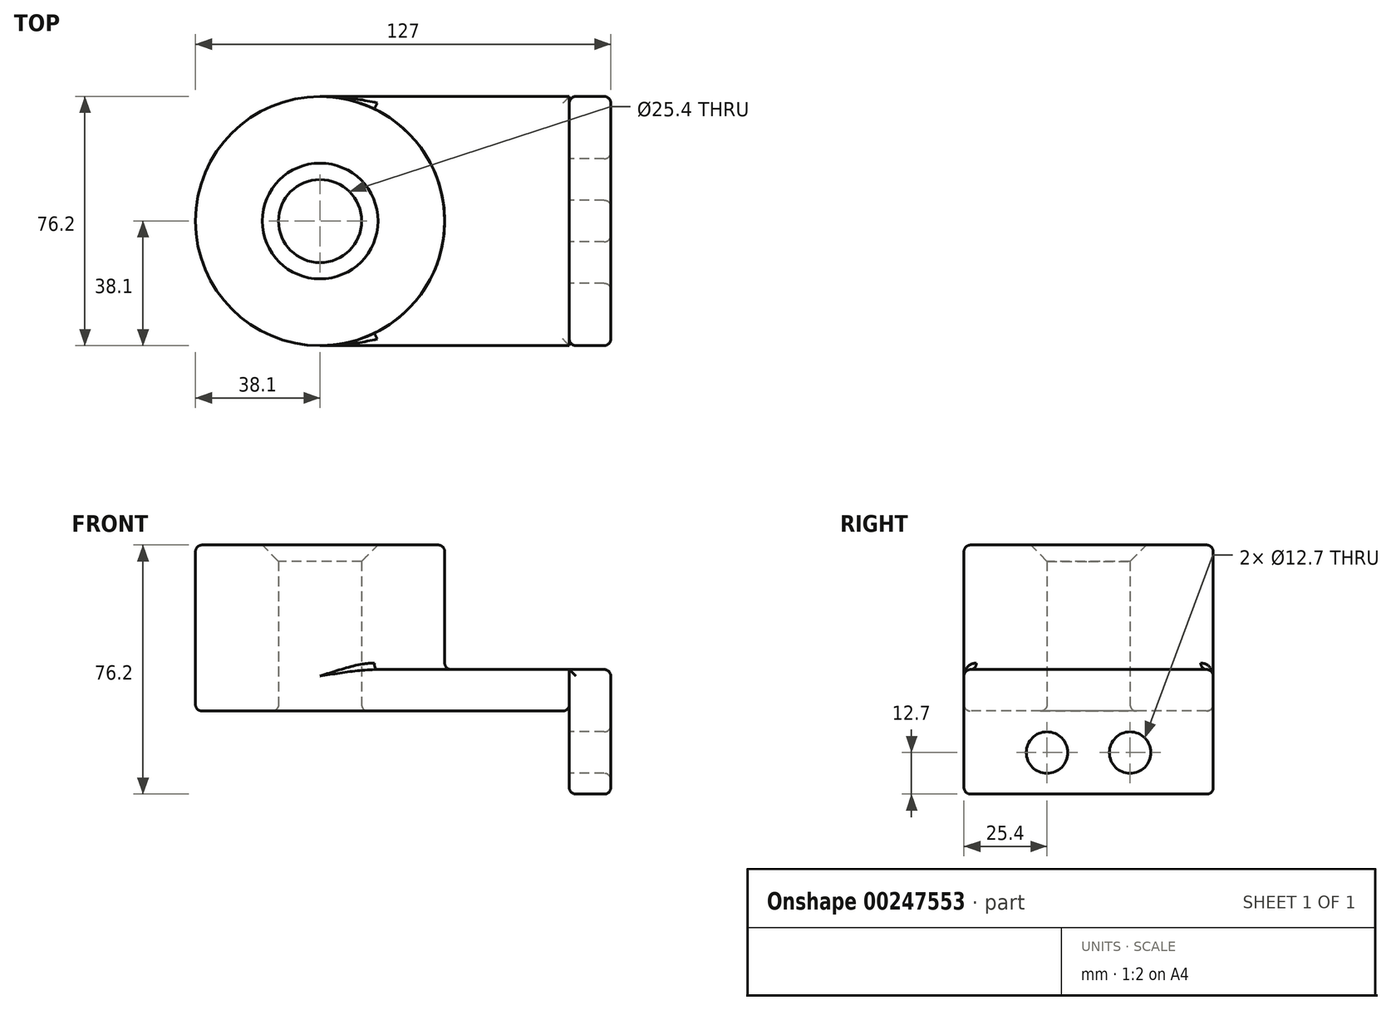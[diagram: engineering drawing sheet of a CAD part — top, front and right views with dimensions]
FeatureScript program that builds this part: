
annotation { "Feature Type Name" : "Feature", "Feature Type Description" : "" }
export const myFeature = defineFeature(function(context is Context, id is Id, definition is map)
    precondition{}
    {
        {
            var Q0;
            Q0=qCreatedBy(makeId("Top.planeOp"),FACE);
            var sketch = newSketch(context, id + "F0", { "sketchPlane" : qUnion([Q0])});
            skLineSegment(sketch, "E0.bottom", {"start": v(38.1, 38.1) * mm, "end": v(-38.1, 38.1) * mm});
            skLineSegment(sketch, "E0.top", {"start": v(38.1, -38.1) * mm, "end": v(-38.1, -38.1) * mm});
            skLineSegment(sketch, "E0.left", {"start": v(38.1, 38.1) * mm, "end": v(38.1, -38.1) * mm});
            skLineSegment(sketch, "E0.right", {"start": v(-38.1, 38.1) * mm, "end": v(-38.1, -38.1) * mm});
            skPoint(sketch, "E0.middle", {"position": v(0, 0) * mm});
            skCircle(sketch, "E1", {"center": v(-38.1, 0) * mm, "radius": 38.1 * mm});
            skCircle(sketch, "E2", {"center": v(-38.1, 0) * mm, "radius": 12.7 * mm});
            skSolve(sketch);
        }
        {
            var Q0;
            Q0 = qSketchRegion(id + "F0", true);
            extrude(context, id + "F1", {"entities" : qUnion([Q0]), "depth" : 12.7 * mm});
        }
        {
            var Q0;
            {var subQ1=sQuery(id+"F0.wireOp",EDGE,"E0.right");var subQ3=sQuery(id+"F0.wireOp",EDGE,"E2");var subQ4=makeQuery(id+"F0.imprint","INTERSECT",VERTEX,{"disambiguationData":[OD(0.0)],"derivedFrom":[subQ1,subQ3]});Q0=makeQuery(id+"F0.imprint","IMPRINT",FACE,{"disambiguationData":[TD([[makeQuery(id+"F0.imprint","IMPRINT",EDGE,{"disambiguationData":[TD([[subQ4,1.0]])],"derivedFrom":subQ3}),-1.0]])]});}
            var Q1;
            {var subQ1=sQuery(id+"F0.wireOp",EDGE,"E0.right");var subQ3=sQuery(id+"F0.wireOp",EDGE,"E2");var subQ4=makeQuery(id+"F0.imprint","INTERSECT",VERTEX,{"disambiguationData":[OD(0.0)],"derivedFrom":[subQ1,subQ3]});Q1=makeQuery(id+"F0.imprint","IMPRINT",FACE,{"disambiguationData":[TD([[makeQuery(id+"F0.imprint","IMPRINT",EDGE,{"disambiguationData":[TD([[subQ4,-1.0]])],"derivedFrom":subQ3}),-1.0]])]});}
            extrude(context, id + "F2", {"entities" : qUnion([Q0, Q1]), "operationType" : NewBodyOperationType.ADD, "depth" : 50.8 * mm});
        }
        {
            var Q0;
            Q0=makeQuery(id+"F1.opExtrude","SWEPT_FACE",FACE,{"disambiguationData":[OSD([sQuery(id+"F0.wireOp",EDGE,"E0.left")])]});
            var sketch = newSketch(context, id + "F3", { "sketchPlane" : qUnion([Q0])});
            skLineSegment(sketch, "E3.bottom", {"start": v(-38.1, 12.7) * mm, "end": v(38.1, 12.7) * mm});
            skLineSegment(sketch, "E3.top", {"start": v(-38.1, -25.4) * mm, "end": v(38.1, -25.4) * mm});
            skLineSegment(sketch, "E3.left", {"start": v(-38.1, 12.7) * mm, "end": v(-38.1, -25.4) * mm});
            skLineSegment(sketch, "E3.right", {"start": v(38.1, 12.7) * mm, "end": v(38.1, -25.4) * mm});
            skLineSegment(sketch, "E4", {"start": v(0, 12.7) * mm, "end": v(0, -52.81) * mm, "construction": true});
            skPoint(sketch, "E4.endSnap0", {"position": v(0, 12.7) * mm});
            skCircle(sketch, "E5", {"center": v(-12.7, -12.7) * mm, "radius": 6.35 * mm});
            skCircle(sketch, "E6.MirrorC", {"center": v(12.7, -12.7) * mm, "radius": 6.35 * mm});
            skSolve(sketch);
        }
        {
            var Q0;
            {var subQ2=sQuery(id+"F3.wireOp",EDGE,"E3.top");Q0=makeQuery(id+"F3.imprint","IMPRINT",FACE,{"disambiguationData":[TD([[makeQuery(id+"F3.imprint","IMPRINT",EDGE,{"derivedFrom":subQ2}),1.0]])]});}
            var Q1;
            {var subQ0=sQuery(id+"F3.wireOp",EDGE,"E3.bottom");Q1=makeQuery(id+"F3.imprint","IMPRINT",FACE,{"disambiguationData":[TD([[makeQuery(id+"F3.imprint","IMPRINT",EDGE,{"derivedFrom":subQ0}),1.0]])]});}
            extrude(context, id + "F4", {"entities" : qUnion([Q0, Q1]), "depth" : 12.7 * mm});
        }
        {
            var Q0;
            Q0=makeQuery(id+"F1.opExtrude","CAP_EDGE",EDGE,{"disambiguationData":[OSD([sQuery(id+"F0.wireOp",EDGE,"E0.top")])],"isStart":false});
            var Q1;
            Q1=makeQuery(id+"F1.opExtrude","CAP_EDGE",EDGE,{"disambiguationData":[OSD([sQuery(id+"F0.wireOp",EDGE,"E0.bottom")])],"isStart":false});
            var Q2;
            {var subQ0=sQuery(id+"F0.wireOp",EDGE,"E1");Q2=makeQuery(id+"F2.boolean.opBoolean","INTERSECT",EDGE,{"derivedFrom":[makeQuery(id+"F1.opExtrude","CAP_FACE",FACE,{"disambiguationData":[OSD([sQuery(id+"F0.wireOp",EDGE,"E0.bottom"),sQuery(id+"F0.wireOp",EDGE,"E0.top"),sQuery(id+"F0.wireOp",EDGE,"E0.left"),subQ0,sQuery(id+"F0.wireOp",EDGE,"E2")])],"isStart":false}),makeQuery(id+"F2.opExtrude","SWEPT_FACE",FACE,{"disambiguationData":[OSD([subQ0])]})]});}
            var Q3;
            Q3=makeQuery(id+"F1.opExtrude","CAP_EDGE",EDGE,{"disambiguationData":[OSD([sQuery(id+"F0.wireOp",EDGE,"E0.top")])],"isStart":true});
            var Q4;
            Q4=makeQuery(id+"F4.opExtrude","CAP_EDGE",EDGE,{"disambiguationData":[OSD([sQuery(id+"F3.wireOp",EDGE,"E3.bottom")])],"isStart":false});
            var Q5;
            Q5=makeQuery(id+"F4.opExtrude","SWEPT_EDGE",EDGE,{"disambiguationData":[OSD([sQuery(id+"F3.wireOp",EDGE,"E3.bottom"),sQuery(id+"F3.wireOp",EDGE,"E3.left")])]});
            var Q6;
            Q6=makeQuery(id+"F4.opExtrude","SWEPT_FACE",FACE,{"disambiguationData":[OSD([sQuery(id+"F3.wireOp",EDGE,"E3.left")])]});
            var Q7;
            Q7=makeQuery(id+"F4.opExtrude","CAP_FACE",FACE,{"disambiguationData":[OSD([sQuery(id+"F3.wireOp",EDGE,"E3.bottom"),sQuery(id+"F3.wireOp",EDGE,"E3.top"),sQuery(id+"F3.wireOp",EDGE,"E3.left"),sQuery(id+"F3.wireOp",EDGE,"E3.right"),sQuery(id+"F3.wireOp",EDGE,"E5"),sQuery(id+"F3.wireOp",EDGE,"E6.MirrorC")])],"isStart":false});
            var Q8;
            Q8=makeQuery(id+"F4.opExtrude","SWEPT_FACE",FACE,{"disambiguationData":[OSD([sQuery(id+"F3.wireOp",EDGE,"E3.right")])]});
            var Q9;
            Q9=makeQuery(id+"F4.opExtrude","SWEPT_FACE",FACE,{"disambiguationData":[OSD([sQuery(id+"F3.wireOp",EDGE,"E3.top")])]});
            var Q10;
            Q10=makeQuery(id+"F1.opExtrude","CAP_FACE",FACE,{"disambiguationData":[OSD([sQuery(id+"F0.wireOp",EDGE,"E0.bottom"),sQuery(id+"F0.wireOp",EDGE,"E0.top"),sQuery(id+"F0.wireOp",EDGE,"E0.left"),sQuery(id+"F0.wireOp",EDGE,"E1"),sQuery(id+"F0.wireOp",EDGE,"E2")])],"isStart":true});
            var Q11;
            Q11=makeQuery(id+"F2.opExtrude","CAP_EDGE",EDGE,{"disambiguationData":[OSD([sQuery(id+"F0.wireOp",EDGE,"E1")])],"isStart":false});
            var Q12;
            {var subQ0=sQuery(id+"F0.wireOp",EDGE,"E1");Q12=makeQuery(id+"F2.boolean.opBoolean","MERGE",FACE,{"derivedFrom":[makeQuery(id+"F1.opExtrude","SWEPT_FACE",FACE,{"disambiguationData":[OSD([subQ0])]}),makeQuery(id+"F2.opExtrude","SWEPT_FACE",FACE,{"disambiguationData":[OSD([subQ0])]})]});}
            var Q13;
            Q13=makeQuery(id+"F1.opExtrude","CAP_EDGE",EDGE,{"disambiguationData":[OSD([sQuery(id+"F0.wireOp",EDGE,"E0.left")])],"isStart":true});
            fillet(context, id + "F5", {"entities" : qUnion([Q0, Q1, Q2, Q3, Q4, Q5, Q6, Q7, Q8, Q9, Q10, Q11, Q12, Q13]), "radius" : 2 * mm, "tangentPropagation" : true, "allowEdgeOverflow" : false});
        }
        {
            var Q0;
            {var subQ0=sQuery(id+"F0.wireOp",EDGE,"E2");Q0=makeQuery(id+"F2.boolean.opBoolean","MERGE",FACE,{"derivedFrom":[makeQuery(id+"F1.opExtrude","SWEPT_FACE",FACE,{"disambiguationData":[OSD([subQ0])]}),makeQuery(id+"F2.opExtrude","SWEPT_FACE",FACE,{"disambiguationData":[OSD([subQ0])]})]});}
            chamfer(context, id + "F6", {"entities" : qUnion([Q0]), "width" : 5 * mm, "tangentPropagation" : true});
        }
    });
